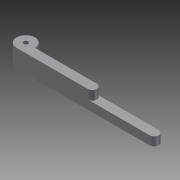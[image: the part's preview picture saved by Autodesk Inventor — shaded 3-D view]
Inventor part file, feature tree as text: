
AUTODESK INVENTOR PART (.ipt)
format: ipt  version: 2011 (Build 150239000, 239)  size: 103,936 bytes
history: native  units: mm
features: fillet x3, sketch x3, extrude x2, other x1, hole x1
ambient origin geometry x8: Origin, YZ Plane, XZ Plane, XY Plane, X Axis, Y Axis, Z Axis, Center Point
feature tree (10):
  other  "Sólido1"
  extrude  "Extrusión1"  Depth=28.0mm
  fillet  "Empalme8"  Radius=2.0mm
  fillet  "Empalme9"  Radius=1.9mm
  hole  "Hole2"  [1 undecoded]
  extrude  "Extrusión3"  Depth=14.5mm
  fillet  "Empalme10"  Radius=2.0mm
  sketch  "Boceto1"  dims[d0=4.0mm d2=28.0mm d3=2.0mm d4=1.9mm d5=0.0mm]
  sketch  "Boceto5"  dims[d23=4.0mm d24=2.0mm]
  sketch  "Boceto6"  dims[d25=1.0mm d27=1.0mm d28=6.0mm d29=4.0mm d30=2.0mm d31=90.0deg d32=8.0mm d33=20.594885mm d34=14.5mm d35=2.0mm d36=0.0mm d37=1.0mm]
note: 1 required parameter value undecoded (feature->parameter linkage not recoverable at this tier; creation-order binding heuristic only, values carry confidence <= 0.55)
